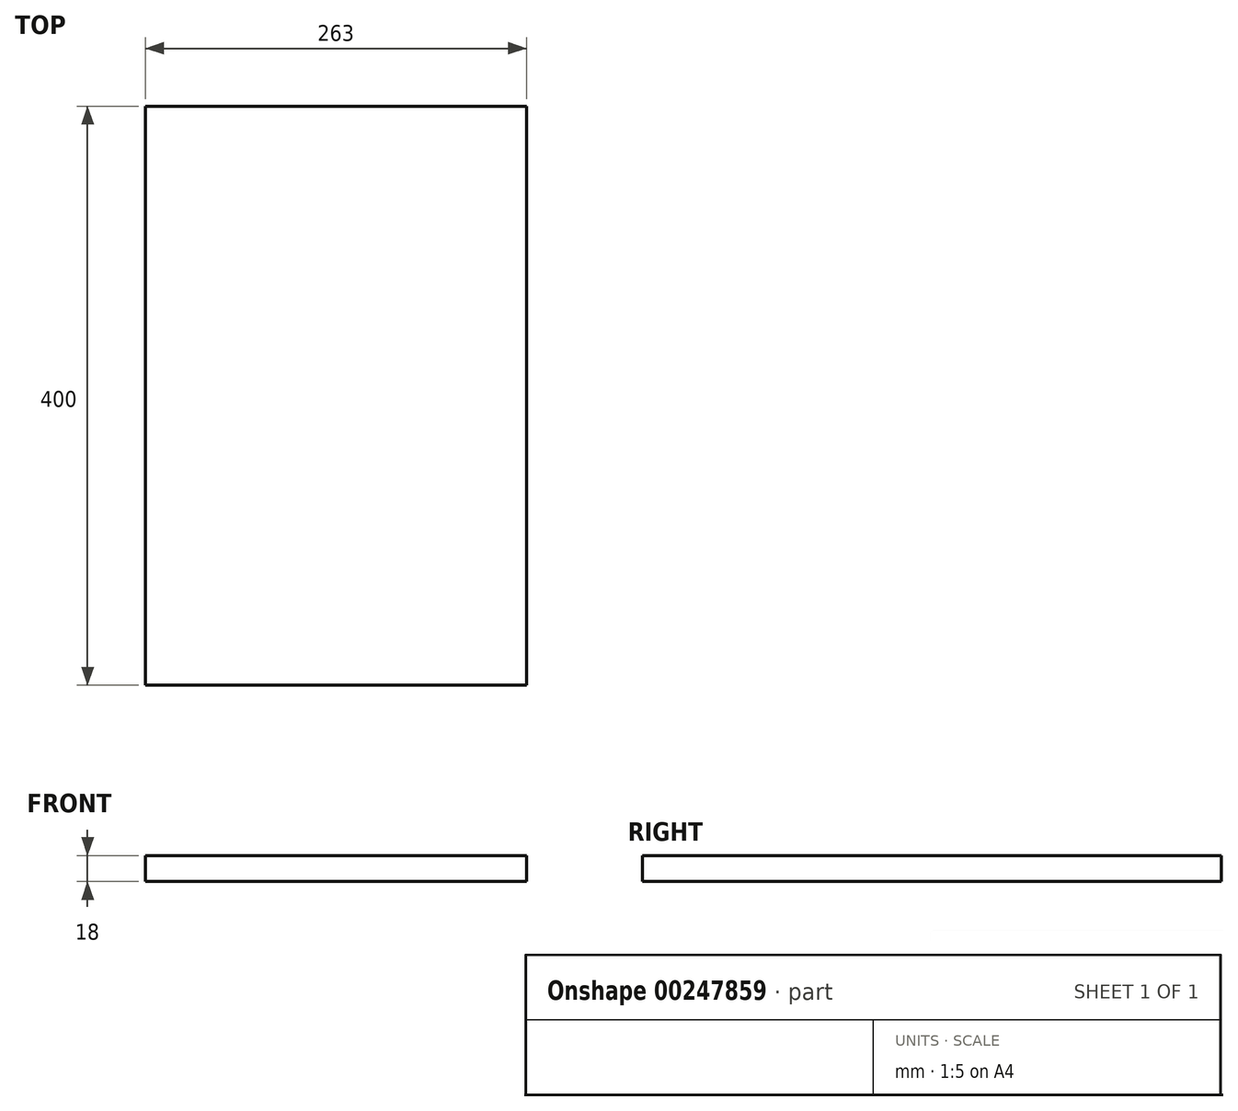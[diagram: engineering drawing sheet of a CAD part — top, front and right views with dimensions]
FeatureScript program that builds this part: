
annotation { "Feature Type Name" : "Feature", "Feature Type Description" : "" }
export const myFeature = defineFeature(function(context is Context, id is Id, definition is map)
    precondition{}
    {
        {
            var Q0;
            Q0=qCreatedBy(makeId("Top.planeOp"),FACE);
            var sketch = newSketch(context, id + "F1", { "sketchPlane" : qUnion([Q0])});
            skLineSegment(sketch, "E0.bottom", {"start": v(0, 0) * mm, "end": v(263, 0) * mm});
            skLineSegment(sketch, "E0.top", {"start": v(0, 400) * mm, "end": v(263, 400) * mm});
            skLineSegment(sketch, "E0.left", {"start": v(0, 0) * mm, "end": v(0, 400) * mm});
            skLineSegment(sketch, "E0.right", {"start": v(263, 0) * mm, "end": v(263, 400) * mm});
            skSolve(sketch);
        }
        {
            var Q0;
            Q0=makeQuery(id+"F1.imprint","IMPRINT",FACE,{"disambiguationData":[TD([[makeQuery(id+"F1.imprint","IMPRINT",EDGE,{"derivedFrom":sQuery(id+"F1.wireOp",EDGE,"E0.bottom")}),1.0]])]});
            extrude(context, id + "F0", {"entities" : qUnion([Q0]), "depth" : 18 * mm});
        }
    });
